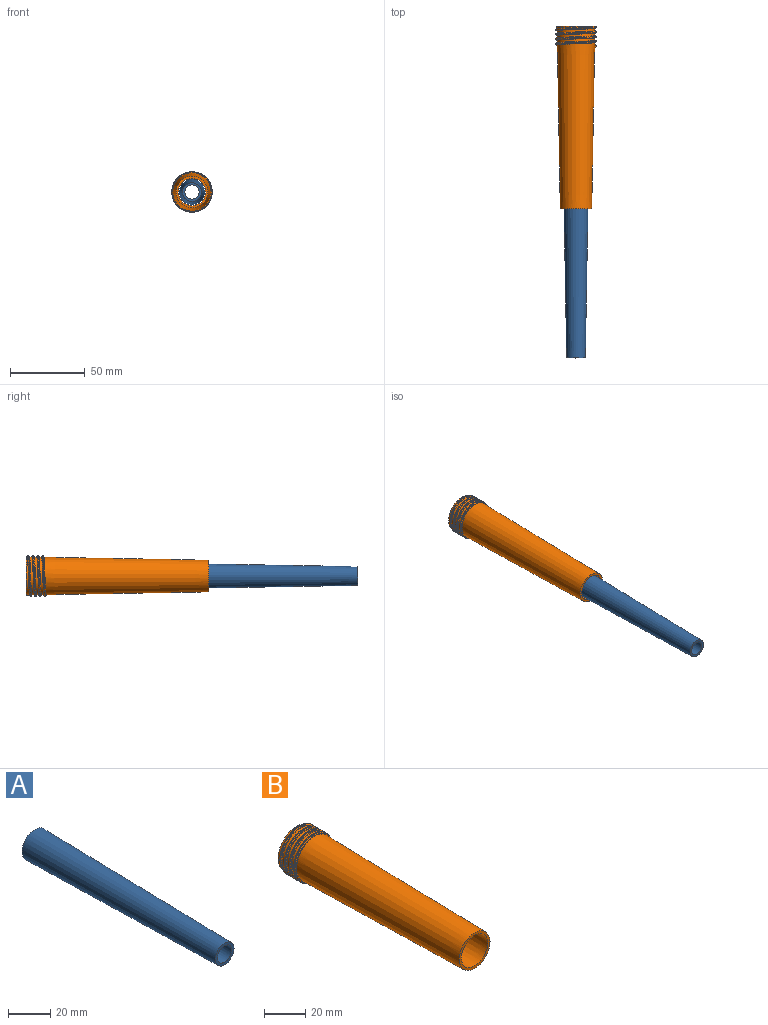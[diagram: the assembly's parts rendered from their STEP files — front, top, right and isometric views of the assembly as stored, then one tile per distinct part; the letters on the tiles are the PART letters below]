
ASSEMBLY  parts=2 mates=1
PART A: 4 faces, bbox 17x127x17 mm
  f0: cone r=8.48mm half-angle=89deg, axis (0,-1,0), area 73.9mm2, adj f2,f3
  f1: cone r=6.26mm half-angle=89deg, axis (0,-1,0), area 52.7mm2, adj f2,f3
  f2: cone r=8.48mm half-angle=1deg, axis (0,1,0), area 5881.2mm2, adj f0,f1
  f3: cone r=6.95mm half-angle=1deg, axis (0,1,0), area 4665.1mm2, adj f0,f1
PART B: 20 faces, bbox 27x121.9x31.1 mm
  f0: cone r=12.7mm half-angle=1deg, axis (0,1,0), area 7947.7mm2, adj f1,f7,f8,f9,f13
  f1: cone r=12.7mm half-angle=1deg, axis (0,1,0), area 130mm2, adj f0,f2,f8,f9
  f2: cone r=12.7mm half-angle=1deg, axis (0,1,0), area 130.6mm2, adj f1,f3,f8,f9
  f3: cone r=12.7mm half-angle=1deg, axis (0,1,0), area 225mm2, adj f2,f5,f6,f8,f9,f11,f12
  f4: cone r=11.18mm half-angle=1deg, axis (0,1,0), area 7747.2mm2, adj f5,f13
  f5: plane 25.4x25.4mm, normal (0,1,0), area 114.3mm2, adj f3,f4
  f6: plane 0.99x0.8mm, normal (0,0,-1), area 0.7mm2, adj f3,f10,f11,f12,f14,f15,f17,f18
  f7: plane 1.53x1.01mm, normal (0,0,1), area 1.3mm2, adj f0,f8,f9,f10,f14,f15,f16,f17
  f8: bspline ~31.09x26.92mm, area 82.8mm2, adj f0,f1,f2,f3,f7,f11,f16
  f9: bspline ~31.09x26.92mm, area 91.2mm2, adj f0,f1,f2,f3,f7,f12,f19
  f10: cylinder r=13.46mm len=26.92mm, axis (0,-1,0), area 99.9mm2, adj f6,f7,f17,f18
  f11: bspline ~0.56x0.53mm, area 0.3mm2, adj f3,f6,f8,f15,f16
  f12: bspline ~0.85x0.51mm, area 0.2mm2, adj f3,f6,f9,f14,f19
  f13: plane 21.14x21.14mm, normal (0,-1,0), area 93.9mm2, adj f0,f4
  f14: bspline ~26.93x26.93mm, area 168.8mm2, adj f6,f7,f12,f18,f19
  f15: bspline ~26.76x26.75mm, area 168.7mm2, adj f6,f7,f11,f16,f17
  f16: bspline ~26.07x26.07mm, area 64.3mm2, adj f7,f8,f11,f15
  f17: bspline ~26.93x26.93mm, area 67.4mm2, adj f6,f7,f10,f15
  f18: bspline ~26.93x26.93mm, area 67.4mm2, adj f6,f7,f10,f14
  f19: bspline ~26.07x26.07mm, area 64.8mm2, adj f7,f9,f12,f14
PLACE A t=(-89.83,96.72,-45.35)mm
PLACE B t=(-89.83,69.18,-45.35)mm fixed
MATE slider A.f0 <-> B.f0  axis (0,1,0) through (-89.83,-88.7,-45.35)mm
